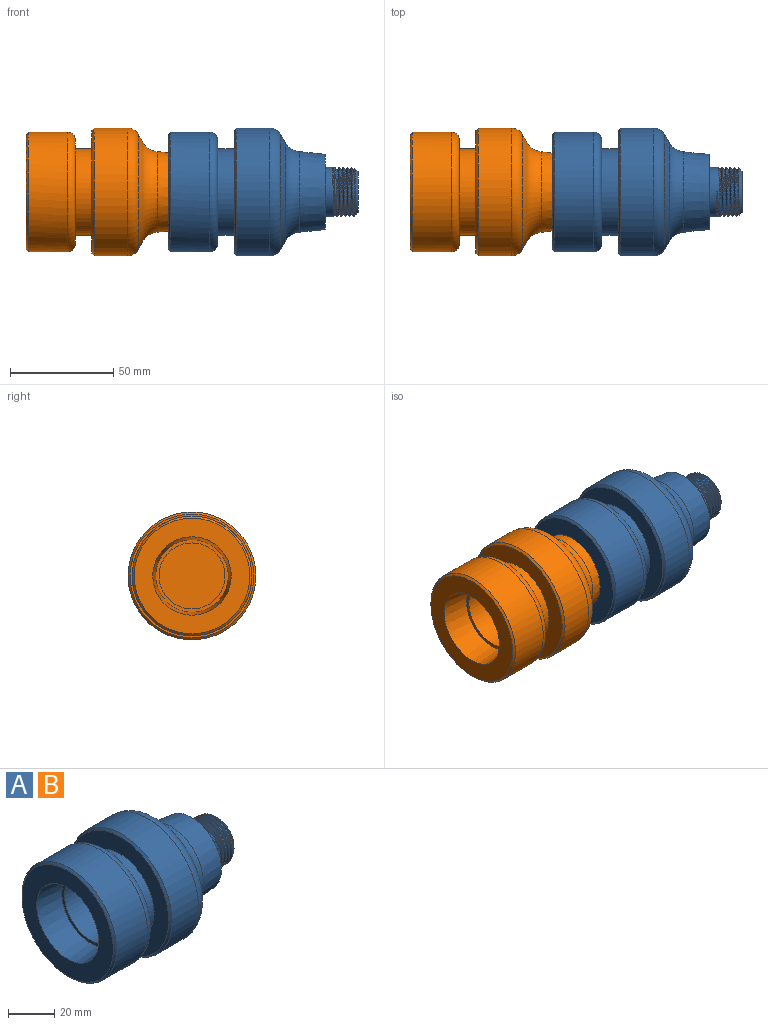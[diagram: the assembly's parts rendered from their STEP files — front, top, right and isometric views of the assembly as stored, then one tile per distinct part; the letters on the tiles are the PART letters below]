
ASSEMBLY  parts=2 mates=1
PART A: 32 faces, bbox 92x67.1x67.1 mm
  f0: cylinder r=12mm len=24mm, axis (-1,0,0), area 364mm2, adj f4,f6,f23,f24,f25,f28
  f1: cylinder r=12mm len=24mm, axis (-1,0,0), area 10.6mm2, adj f2,f27,f28,f30
  f2: cylinder r=12mm len=24mm, axis (-1,0,0), area 18.8mm2, adj f1,f3,f27,f28
  f3: cylinder r=12mm len=24mm, axis (-1,0,0), area 18.8mm2, adj f2,f4,f27,f28
  f4: cylinder r=12mm len=24mm, axis (-1,0,0), area 18.8mm2, adj f0,f3,f27,f28
  f5: plane 32x32mm, normal (-1,0,0), area 804.2mm2, adj f18
  f6: plane 36.6x36.6mm, normal (1,0,0), area 599.7mm2, adj f0,f7
  f7: cone r=20mm half-angle=5.7deg, axis (-1,0,0), area 1482.5mm2, adj f6,f22
  f8: cone r=31mm half-angle=60deg, axis (-1,0,0), area 755.2mm2, adj f21,f22
  f9: cylinder r=31mm len=62mm, axis (-1,0,0), area 3152.5mm2, adj f20,f21
  f10: plane 60x60mm, normal (-1,0,0), area 1442mm2, adj f11,f20
  f11: cylinder r=21mm len=42mm, axis (-1,0,0), area 1055.6mm2, adj f10,f12
  f12: plane 50x50mm, normal (1,0,0), area 578.1mm2, adj f11,f13
  f13: torus R=25mm, axis (-1,0,0), area 1087.5mm2, adj f12,f14
  f14: cylinder r=29mm len=58mm, axis (-1,0,0), area 3462mm2, adj f13,f19
  f15: plane 56x56mm, normal (-1,0,0), area 1328.9mm2, adj f16,f19
  f16: cone r=17.6mm half-angle=5.7deg, axis (-1,0,0), area 1617.8mm2, adj f15,f17
  f17: plane 35.2x35.2mm, normal (-1,0,0), area 168.9mm2, adj f16,f18
  f18: cylinder r=16mm len=32mm, axis (-1,0,0), area 2412.7mm2, adj f5,f17
  f19: cone r=28mm half-angle=45deg, axis (1,0,0), area 253.2mm2, adj f14,f15
  f20: cone r=30mm half-angle=45deg, axis (1,0,0), area 271mm2, adj f9,f10
  f21: torus R=25mm, axis (1,0,0), area 1182.9mm2, adj f8,f9
  f22: torus R=28.5mm, axis (-1,0,0), area 1136.8mm2, adj f7,f8
  f23: plane 0.61x0.2mm, normal (0,-1,0), area 0.1mm2, adj f0,f24,f25,f29
  f24: bspline ~25.6x25.19mm, area 49.2mm2, adj f0,f23,f27,f29
  f25: bspline ~25.6x25.19mm, area 49.2mm2, adj f0,f23,f28,f29
  f26: bspline ~25.21x21.84mm, area 176.1mm2, adj f27,f28,f29,f30
  f27: bspline ~27.71x24mm, area 364.2mm2, adj f1,f2,f3,f4,f24,f26,f30
  f28: bspline ~27.71x24mm, area 415.1mm2, adj f0,f1,f2,f3,f4,f25,f26,f30
  f29: bspline ~23.42x23.01mm, area 39.9mm2, adj f23,f24,f25,f26
  f30: cone r=12mm half-angle=45deg, axis (-1,0,0), area 132.6mm2, adj f1,f26,f27,f28,f31
  f31: plane 20x20mm, normal (1,0,0), area 314.2mm2, adj f30
PART B: same geometry as A
PLACE A at identity fixed
PLACE B t=(-69,0,0)mm
MATE planar A.f0 <-> B.f0  axis (-1,0,0) through (-92,0,0)mm
